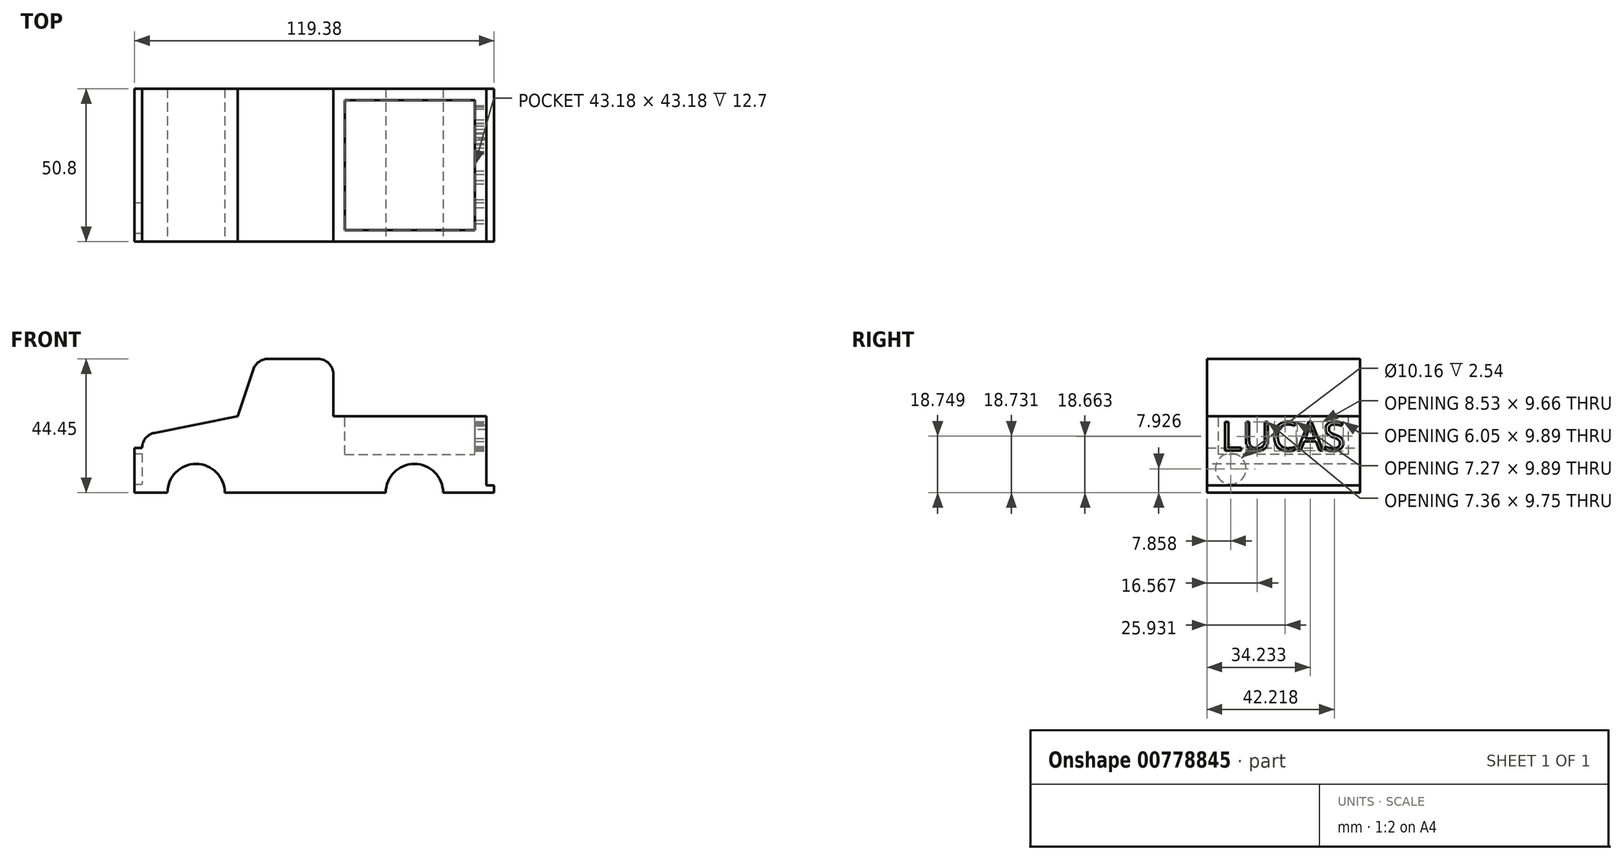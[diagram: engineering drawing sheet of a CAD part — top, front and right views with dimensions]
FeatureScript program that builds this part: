
annotation { "Feature Type Name" : "Feature", "Feature Type Description" : "" }
export const myFeature = defineFeature(function(context is Context, id is Id, definition is map)
    precondition{}
    {
        {
            var Q0;
            Q0=qCreatedBy(makeId("Front.planeOp"),FACE);
            var sketch = newSketch(context, id + "F0", { "sketchPlane" : qUnion([Q0])});
            skLineSegment(sketch, "E0.bottom", {"start": v(0, 0) * mm, "end": v(50.8, 0) * mm});
            skLineSegment(sketch, "E0.top", {"start": v(0, -25.4) * mm, "end": v(50.8, -25.4) * mm});
            skLineSegment(sketch, "E0.left", {"start": v(0, 0) * mm, "end": v(0, -25.4) * mm});
            skLineSegment(sketch, "E0.right", {"start": v(50.8, 0) * mm, "end": v(50.8, -25.4) * mm});
            skLineSegment(sketch, "E1.bottom", {"start": v(0, -25.4) * mm, "end": v(-25.4, -25.4) * mm});
            skLineSegment(sketch, "E1.top", {"start": v(0, 19.05) * mm, "end": v(-25.4, 19.05) * mm});
            skLineSegment(sketch, "E1.left", {"start": v(0, -25.4) * mm, "end": v(0, 19.05) * mm});
            skLineSegment(sketch, "E1.right", {"start": v(-25.4, -25.4) * mm, "end": v(-25.4, 19.05) * mm});
            skLineSegment(sketch, "E2", {"start": v(-25.4, -25.4) * mm, "end": v(-63.5, -25.4) * mm});
            skLineSegment(sketch, "E3", {"start": v(-63.5, -25.4) * mm, "end": v(-63.5, -6.35) * mm});
            skLineSegment(sketch, "E4", {"start": v(-25.4, 0) * mm, "end": v(-31.75, 0) * mm});
            skLineSegment(sketch, "E5", {"start": v(-25.4, 19.05) * mm, "end": v(-31.75, 0) * mm});
            skLineSegment(sketch, "E6", {"start": v(-63.5, -6.35) * mm, "end": v(-31.75, 0) * mm});
            skSolve(sketch);
        }
        {
            var Q0;
            Q0 = qSketchRegion(id + "F0", true);
            extrude(context, id + "F1", {"entities" : qUnion([Q0]), "depth" : 50.8 * mm, "offsetDistance" : 25.4 * mm});
        }
        {
            var Q0;
            Q0=makeQuery(id+"F1.opExtrude","SWEPT_EDGE",EDGE,{"disambiguationData":[OSD([sQuery(id+"F0.wireOp",EDGE,"E1.top"),sQuery(id+"F0.wireOp",EDGE,"E1.right"),sQuery(id+"F0.wireOp",EDGE,"E5")])]});
            var Q1;
            Q1=makeQuery(id+"F1.opExtrude","SWEPT_EDGE",EDGE,{"disambiguationData":[OSD([sQuery(id+"F0.wireOp",EDGE,"E3"),sQuery(id+"F0.wireOp",EDGE,"E6")])]});
            fillet(context, id + "F2", {"entities" : qUnion([Q0, Q1]), "radius" : 5.08 * mm, "tangentPropagation" : true, "allowEdgeOverflow" : false});
        }
        {
            var Q0;
            Q0=makeQuery(id+"F1.opExtrude","SWEPT_EDGE",EDGE,{"disambiguationData":[OSD([sQuery(id+"F0.wireOp",EDGE,"E1.top"),sQuery(id+"F0.wireOp",EDGE,"E1.left")])]});
            fillet(context, id + "F3", {"entities" : qUnion([Q0]), "radius" : 5.08 * mm, "tangentPropagation" : true, "allowEdgeOverflow" : false});
        }
        {
            var Q0;
            Q0=makeQuery(id+"F1.opExtrude","CAP_FACE",FACE,{"disambiguationData":[OSD([sQuery(id+"F0.wireOp",EDGE,"E0.bottom"),sQuery(id+"F0.wireOp",EDGE,"E0.top"),sQuery(id+"F0.wireOp",EDGE,"E0.right"),sQuery(id+"F0.wireOp",EDGE,"E1.bottom"),sQuery(id+"F0.wireOp",EDGE,"E1.top"),sQuery(id+"F0.wireOp",EDGE,"E1.left"),sQuery(id+"F0.wireOp",EDGE,"E2"),sQuery(id+"F0.wireOp",EDGE,"E3"),sQuery(id+"F0.wireOp",EDGE,"E5"),sQuery(id+"F0.wireOp",EDGE,"E6")])],"isStart":false});
            var sketch = newSketch(context, id + "F4", { "sketchPlane" : qUnion([Q0])});
            skCircle(sketch, "E7", {"center": v(-45.58, -25.4) * mm, "radius": 9.53 * mm});
            skPoint(sketch, "E7.centerSnap0", {"position": v(-45.58, -2.77) * mm});
            skCircle(sketch, "E8", {"center": v(26.9, -25.4) * mm, "radius": 9.53 * mm});
            skSolve(sketch);
        }
        {
            var Q0;
            {var subQ0=sQuery(id+"F4.wireOp",EDGE,"E7");var subQ1=makeQuery(id+"F1.opExtrude","CAP_EDGE",EDGE,{"disambiguationData":[OSD([sQuery(id+"F0.wireOp",EDGE,"E0.top"),sQuery(id+"F0.wireOp",EDGE,"E1.bottom"),sQuery(id+"F0.wireOp",EDGE,"E2")])],"isStart":false});var subQ2=makeQuery(id+"F4.imprint","INTERSECT",VERTEX,{"disambiguationData":[OD(0.0)],"derivedFrom":[subQ1,subQ0]});Q0=makeQuery(id+"F4.imprint","IMPRINT",FACE,{"disambiguationData":[TD([[makeQuery(id+"F4.imprint","IMPRINT",EDGE,{"disambiguationData":[TD([[subQ2,1.0]])],"derivedFrom":subQ0}),1.0]])]});}
            var Q1;
            {var subQ0=sQuery(id+"F4.wireOp",EDGE,"E8");var subQ1=makeQuery(id+"F1.opExtrude","CAP_EDGE",EDGE,{"disambiguationData":[OSD([sQuery(id+"F0.wireOp",EDGE,"E0.top"),sQuery(id+"F0.wireOp",EDGE,"E1.bottom"),sQuery(id+"F0.wireOp",EDGE,"E2")])],"isStart":false});var subQ2=makeQuery(id+"F4.imprint","INTERSECT",VERTEX,{"disambiguationData":[OD(0.0)],"derivedFrom":[subQ1,subQ0]});Q1=makeQuery(id+"F4.imprint","IMPRINT",FACE,{"disambiguationData":[TD([[makeQuery(id+"F4.imprint","IMPRINT",EDGE,{"disambiguationData":[TD([[subQ2,-1.0]])],"derivedFrom":subQ0}),1.0]])]});}
            extrude(context, id + "F5", {"entities" : qUnion([Q0, Q1]), "operationType" : NewBodyOperationType.REMOVE, "oppositeDirection" : true, "depth" : 50.8 * mm, "offsetDistance" : 25.4 * mm});
        }
        {
            var Q0;
            Q0=makeQuery(id+"F1.opExtrude","SWEPT_FACE",FACE,{"disambiguationData":[OSD([sQuery(id+"F0.wireOp",EDGE,"E0.right")])]});
            var sketch = newSketch(context, id + "F6", { "sketchPlane" : qUnion([Q0])});
            skLineSegment(sketch, "E9.bottom", {"start": v(-53.98, -22.97) * mm, "end": v(3.18, -22.97) * mm});
            skLineSegment(sketch, "E9.top", {"start": v(-53.98, -28.05) * mm, "end": v(3.18, -28.05) * mm});
            skLineSegment(sketch, "E9.left", {"start": v(-53.98, -22.97) * mm, "end": v(-53.98, -28.05) * mm});
            skLineSegment(sketch, "E9.right", {"start": v(3.18, -22.97) * mm, "end": v(3.18, -28.05) * mm});
            skSolve(sketch);
        }
        {
            var Q0;
            {var subQ1=sQuery(id+"F0.wireOp",EDGE,"E0.right");var subQ6=makeQuery(id+"F1.opExtrude","SWEPT_EDGE",EDGE,{"disambiguationData":[OSD([sQuery(id+"F0.wireOp",EDGE,"E0.top"),subQ1])]});Q0=makeQuery(id+"F6.imprint","IMPRINT",FACE,{"disambiguationData":[TD([[makeQuery(id+"F6.imprint","IMPRINT",EDGE,{"derivedFrom":subQ6}),1.0]])]});}
            extrude(context, id + "F7", {"entities" : qUnion([Q0]), "operationType" : NewBodyOperationType.ADD, "depth" : 2.54 * mm, "offsetDistance" : 25.4 * mm});
        }
        {
            var Q0;
            Q0=makeQuery(id+"F1.opExtrude","SWEPT_FACE",FACE,{"disambiguationData":[OSD([sQuery(id+"F0.wireOp",EDGE,"E0.bottom")])]});
            var sketch = newSketch(context, id + "F8", { "sketchPlane" : qUnion([Q0])});
            skLineSegment(sketch, "E10.bottom", {"start": v(3.8, -3.8) * mm, "end": v(47, -3.8) * mm});
            skLineSegment(sketch, "E10.top", {"start": v(3.81, -47) * mm, "end": v(47, -47) * mm});
            skLineSegment(sketch, "E10.left", {"start": v(3.8, -3.81) * mm, "end": v(3.81, -47) * mm});
            skLineSegment(sketch, "E10.right", {"start": v(47, -3.81) * mm, "end": v(47, -47) * mm});
            skSolve(sketch);
        }
        {
            var Q0;
            Q0=makeQuery(id+"F8.imprint","IMPRINT",FACE,{"disambiguationData":[TD([[makeQuery(id+"F8.imprint","IMPRINT",EDGE,{"derivedFrom":sQuery(id+"F8.wireOp",EDGE,"E10.bottom")}),-1.0]])]});
            extrude(context, id + "F9", {"entities" : qUnion([Q0]), "operationType" : NewBodyOperationType.REMOVE, "oppositeDirection" : true, "depth" : 12.7 * mm, "offsetDistance" : 25.4 * mm});
        }
        {
            var Q0;
            Q0=makeQuery(id+"F1.opExtrude","SWEPT_FACE",FACE,{"disambiguationData":[OSD([sQuery(id+"F0.wireOp",EDGE,"E3")])]});
            var sketch = newSketch(context, id + "F10", { "sketchPlane" : qUnion([Q0])});
            skCircle(sketch, "E11", {"center": v(7.86, -17.47) * mm, "radius": 5.08 * mm});
            skCircle(sketch, "E12.MirrorC", {"center": v(42.94, -17.47) * mm, "radius": 5.08 * mm});
            skSolve(sketch);
        }
        {
            var Q0;
            Q0=makeQuery(id+"F10.imprint","IMPRINT",FACE,{"disambiguationData":[TD([[makeQuery(id+"F10.imprint","IMPRINT",EDGE,{"derivedFrom":sQuery(id+"F10.wireOp",EDGE,"E11")}),1.0]])]});
            var Q1;
            Q1=makeQuery(id+"F10.imprint","IMPRINT",FACE,{"disambiguationData":[TD([[makeQuery(id+"F10.imprint","IMPRINT",EDGE,{"derivedFrom":sQuery(id+"F10.wireOp",EDGE,"E12.MirrorC")}),-1.0]])]});
            extrude(context, id + "F11", {"entities" : qUnion([Q0, Q1]), "operationType" : NewBodyOperationType.ADD, "depth" : 2.54 * mm, "offsetDistance" : 25.4 * mm});
        }
        {
            var Q0;
            {var subQ0=sQuery(id+"F0.wireOp",EDGE,"E0.right");var subQ1=makeQuery(id+"F1.opExtrude","CAP_EDGE",EDGE,{"disambiguationData":[OSD([subQ0])],"isStart":false});var subQ2=sQuery(id+"F0.wireOp",EDGE,"E0.top");Q0=makeQuery(id+"F7.boolean.opBoolean","MERGE",FACE,{"derivedFrom":[makeQuery(id+"F1.opExtrude","CAP_FACE",FACE,{"disambiguationData":[OSD([sQuery(id+"F0.wireOp",EDGE,"E0.bottom"),subQ2,subQ0,sQuery(id+"F0.wireOp",EDGE,"E1.bottom"),sQuery(id+"F0.wireOp",EDGE,"E1.top"),sQuery(id+"F0.wireOp",EDGE,"E1.left"),sQuery(id+"F0.wireOp",EDGE,"E2"),sQuery(id+"F0.wireOp",EDGE,"E3"),sQuery(id+"F0.wireOp",EDGE,"E5"),sQuery(id+"F0.wireOp",EDGE,"E6")])],"isStart":false}),makeQuery(id+"F7.opExtrude","SWEPT_FACE",FACE,{"disambiguationData":[OSD([subQ0]),TDD([makeQuery(id+"F6.imprint","IMPRINT",EDGE,{"disambiguationData":[TD([[makeQuery(id+"F6.imprint","INTERSECT",VERTEX,{"derivedFrom":[subQ1,sQuery(id+"F6.wireOp",EDGE,"E9.bottom")]}),-1.0]])],"derivedFrom":subQ1})])]})]});}
            var sketch = newSketch(context, id + "F12", { "sketchPlane" : qUnion([Q0])});
            skText(sketch, "E13", { "text": "LUCAS", "fontName": "OpenSans-Regular.ttf"});
            const initialGuessF12  = {"E13": [0.00356, -0.01188, 1, 0, 0.01007]};
            skSetInitialGuess(sketch, initialGuessF12);
            skSolve(sketch);
        }
        {
            var Q0;
            Q0=makeQuery(id+"F1.opExtrude","SWEPT_FACE",FACE,{"disambiguationData":[OSD([sQuery(id+"F0.wireOp",EDGE,"E0.right")])]});
            var sketch = newSketch(context, id + "F13", { "sketchPlane" : qUnion([Q0])});
            skText(sketch, "E14", { "text": "LUCAS", "fontName": "OpenSans-Regular.ttf"});
            skPoint(sketch, "E14.secondSnap0", {"position": v(0, -11.48) * mm});
            const initialGuessF13  = {"E14": [-0.04613, -0.01148, 1, 0, 0.0097]};
            skSetInitialGuess(sketch, initialGuessF13);
            skSolve(sketch);
        }
        {
            var Q0;
            Q0 = qSketchRegion(id + "F13", true);
            extrude(context, id + "F14", {"entities" : qUnion([Q0]), "operationType" : NewBodyOperationType.REMOVE, "oppositeDirection" : true, "depth" : 12.7 * mm, "offsetDistance" : 25.4 * mm});
        }
    });
